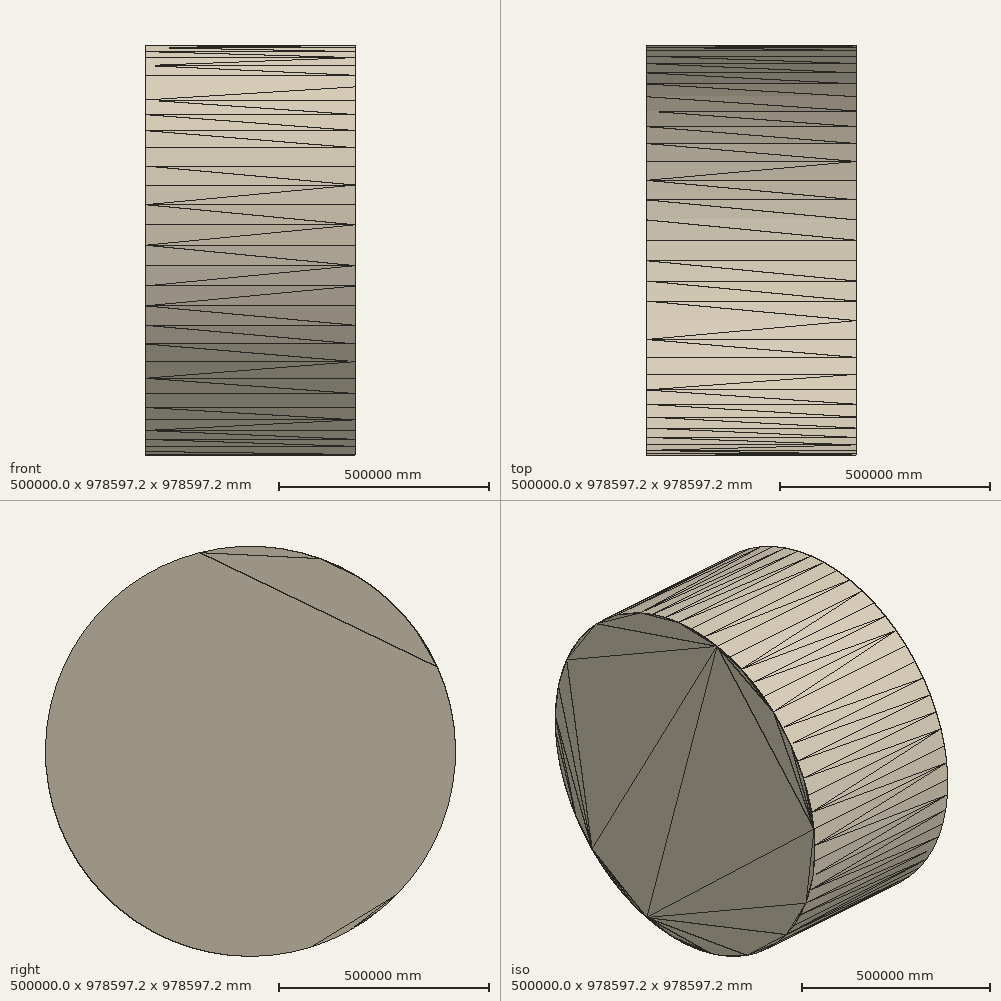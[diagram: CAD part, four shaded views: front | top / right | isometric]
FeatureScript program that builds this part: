
annotation { "Feature Type Name" : "Feature", "Feature Type Description" : "" }
export const myFeature = defineFeature(function(context is Context, id is Id, definition is map)
    precondition{}
    {
        {
            var Q0;
            Q0=qCreatedBy(makeId("Right.planeOp"),FACE);
            var sketch = newSketch(context, id + "F0", { "sketchPlane" : qUnion([Q0])});
            skCircle(sketch, "E0", {"center": v(0, 0) * mm, "radius": 489298.6 * mm});
            skSolve(sketch);
        }
        {
            var Q0;
            Q0 = qSketchRegion(id + "F0", true);
            extrude(context, id + "F1", {"entities" : qUnion([Q0]), "depth" : 500000 * mm, "offsetDistance" : 25.4 * mm});
        }
    });
